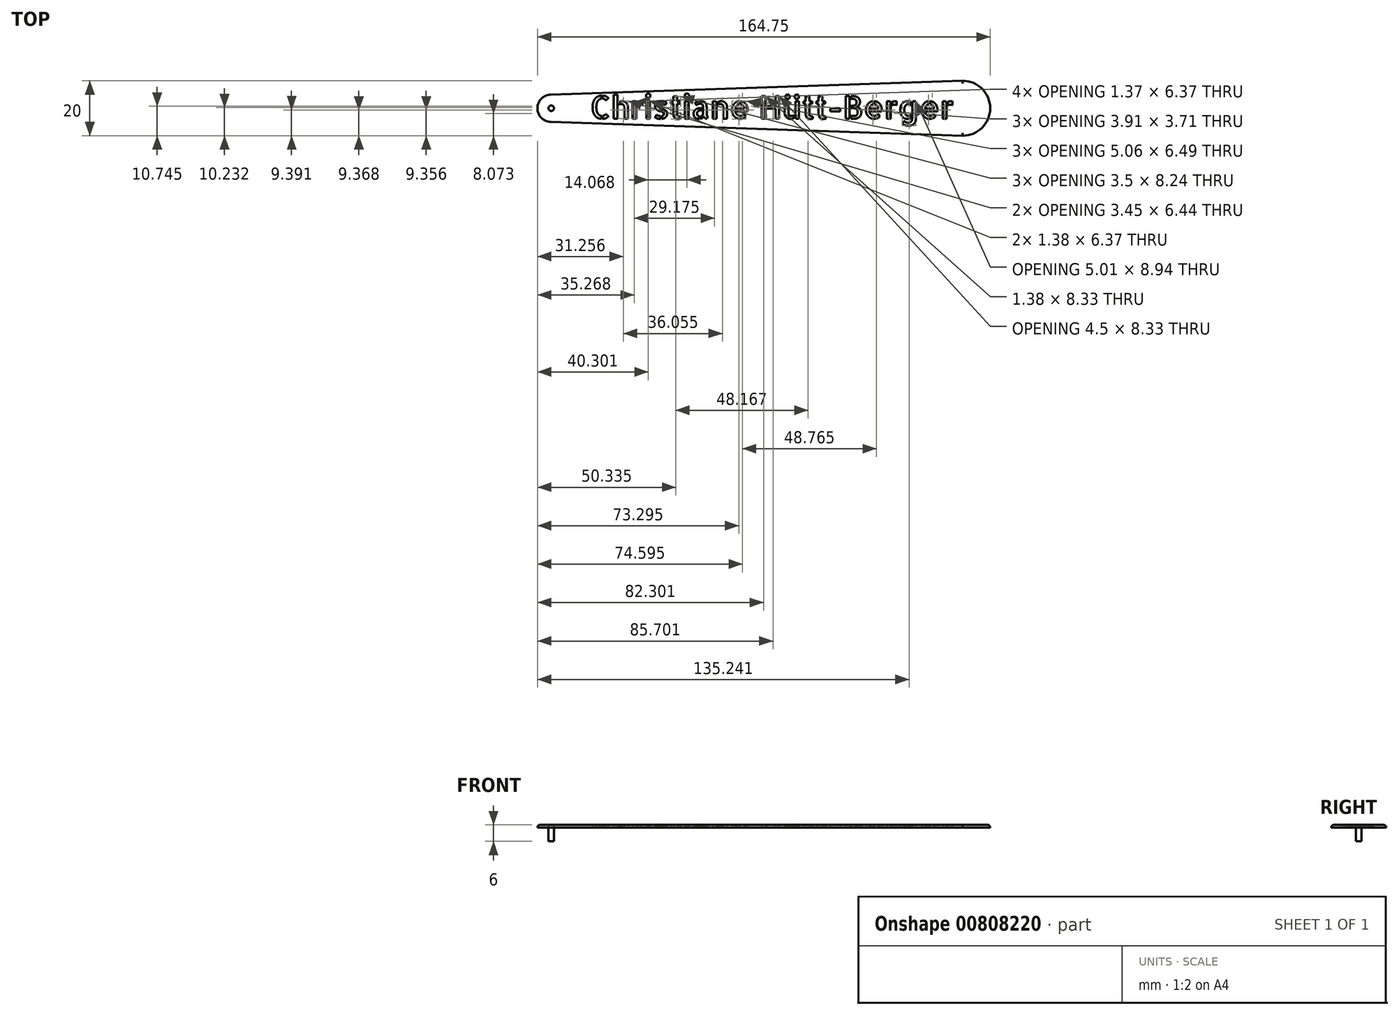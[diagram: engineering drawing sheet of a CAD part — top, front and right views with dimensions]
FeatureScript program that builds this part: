
annotation { "Feature Type Name" : "Feature", "Feature Type Description" : "" }
export const myFeature = defineFeature(function(context is Context, id is Id, definition is map)
    precondition{}
    {
        {
            var Q0;
            Q0=qCreatedBy(makeId("Top.planeOp"),FACE);
            var sketch = newSketch(context, id + "F0", { "sketchPlane" : qUnion([Q0])});
            skCircle(sketch, "E0", {"center": v(0, 0) * mm, "radius": 5 * mm});
            skLineSegment(sketch, "E1", {"start": v(0, 0) * mm, "end": v(149.75, 0) * mm, "construction": true});
            skLineSegment(sketch, "E2", {"start": v(-0.17, -5) * mm, "end": v(149.75, -10) * mm});
            skLineSegment(sketch, "E3", {"start": v(-0.17, 5) * mm, "end": v(149.75, 10) * mm});
            skLineSegment(sketch, "E4", {"start": v(149.75, 10) * mm, "end": v(149.75, -10) * mm, "construction": true});
            skArc(sketch, "E5", {"start": v(149.08, -9.98) * mm, "mid": v(159.75, 0) * mm, "end": v(149.08, 9.98) * mm});
            skCircle(sketch, "E6", {"center": v(0, 0) * mm, "radius": 1 * mm});
            skSolve(sketch);
        }
        {
            var Q0;
            Q0=makeQuery(id+"F0.imprint","IMPRINT",FACE,{"disambiguationData":[TD([[makeQuery(id+"F0.imprint","IMPRINT",EDGE,{"derivedFrom":sQuery(id+"F0.wireOp",EDGE,"AOrL48i1-m9wN-TTek-OaFp-i6hoLE5QwSDf")}),-1.0]])]});
            var Q1;
            {var subQ4=sQuery(id+"F0.wireOp",EDGE,"E0");var subQ8=sQuery(id+"F0.wireOp",EDGE,"E2");var subQ17=makeQuery(id+"F0.imprint","INTERSECT",VERTEX,{"derivedFrom":[subQ4,subQ8]});Q1=makeQuery(id+"F0.imprint","IMPRINT",FACE,{"disambiguationData":[TD([[makeQuery(id+"F0.imprint","IMPRINT",EDGE,{"disambiguationData":[TD([[subQ17,-1.0]])],"derivedFrom":subQ4}),-1.0]])]});}
            var Q2;
            {var subQ1=sQuery(id+"F0.wireOp",EDGE,"429c22a2-0887-486a-967f-2b94e1a87693");var subQ8=sQuery(id+"F0.wireOp",EDGE,"E0");var subQ9=makeQuery(id+"F0.imprint","INTERSECT",VERTEX,{"derivedFrom":[subQ8,subQ1]});Q2=makeQuery(id+"F0.imprint","IMPRINT",FACE,{"disambiguationData":[TD([[makeQuery(id+"F0.imprint","IMPRINT",EDGE,{"disambiguationData":[TD([[subQ9,-1.0]])],"derivedFrom":subQ8}),-1.0]])]});}
            var Q3;
            {var subQ0=sQuery(id+"F0.wireOp",EDGE,"9d5f52ef-638e-458b-9d80-165e25f735ae0.MirrorCS");var subQ1=sQuery(id+"F0.wireOp",EDGE,"429c22a2-0887-486a-967f-2b94e1a87693");var subQ2=makeQuery(id+"F0.imprint","INTERSECT",VERTEX,{"disambiguationData":[OD(1.0)],"derivedFrom":[subQ1,subQ0]});Q3=makeQuery(id+"F0.imprint","IMPRINT",FACE,{"disambiguationData":[TD([[makeQuery(id+"F0.imprint","IMPRINT",EDGE,{"disambiguationData":[TD([[subQ2,-1.0]])],"derivedFrom":subQ1}),-1.0]])]});}
            var Q4;
            {var subQ0=sQuery(id+"F0.wireOp",EDGE,"9d5f52ef-638e-458b-9d80-165e25f735ae0.MirrorCS");var subQ1=sQuery(id+"F0.wireOp",EDGE,"429c22a2-0887-486a-967f-2b94e1a87693");var subQ2=makeQuery(id+"F0.imprint","INTERSECT",VERTEX,{"disambiguationData":[OD(2.0)],"derivedFrom":[subQ1,subQ0]});Q4=makeQuery(id+"F0.imprint","IMPRINT",FACE,{"disambiguationData":[TD([[makeQuery(id+"F0.imprint","IMPRINT",EDGE,{"disambiguationData":[TD([[subQ2,-1.0]])],"derivedFrom":subQ1}),1.0]])]});}
            var Q5;
            {var subQ0=sQuery(id+"F0.wireOp",EDGE,"9d5f52ef-638e-458b-9d80-165e25f735ae0.MirrorCS");var subQ1=sQuery(id+"F0.wireOp",EDGE,"429c22a2-0887-486a-967f-2b94e1a87693");var subQ2=makeQuery(id+"F0.imprint","INTERSECT",VERTEX,{"disambiguationData":[OD(0.0)],"derivedFrom":[subQ1,subQ0]});Q5=makeQuery(id+"F0.imprint","IMPRINT",FACE,{"disambiguationData":[TD([[makeQuery(id+"F0.imprint","IMPRINT",EDGE,{"disambiguationData":[TD([[subQ2,1.0]])],"derivedFrom":subQ1}),-1.0]])]});}
            var Q6;
            {var subQ0=sQuery(id+"F0.wireOp",EDGE,"9f0347f5-2bf8-49b9-a686-556642ef9bf0");var subQ1=sQuery(id+"F0.wireOp",EDGE,"9d5f52ef-638e-458b-9d80-165e25f735ae0.MirrorCS");var subQ2=makeQuery(id+"F0.imprint","INTERSECT",VERTEX,{"disambiguationData":[OD(0.0)],"derivedFrom":[subQ1,subQ0]});Q6=makeQuery(id+"F0.imprint","IMPRINT",FACE,{"disambiguationData":[TD([[makeQuery(id+"F0.imprint","IMPRINT",EDGE,{"disambiguationData":[TD([[subQ2,-1.0]])],"derivedFrom":subQ1}),1.0]])]});}
            var Q7;
            {var subQ0=sQuery(id+"F0.wireOp",EDGE,"9f0347f5-2bf8-49b9-a686-556642ef9bf0");var subQ1=sQuery(id+"F0.wireOp",EDGE,"9d5f52ef-638e-458b-9d80-165e25f735ae0.MirrorCS");var subQ2=makeQuery(id+"F0.imprint","INTERSECT",VERTEX,{"disambiguationData":[OD(0.0)],"derivedFrom":[subQ1,subQ0]});Q7=makeQuery(id+"F0.imprint","IMPRINT",FACE,{"disambiguationData":[TD([[makeQuery(id+"F0.imprint","IMPRINT",EDGE,{"disambiguationData":[TD([[subQ2,-1.0]])],"derivedFrom":subQ1}),-1.0]])]});}
            var Q8;
            {var subQ0=sQuery(id+"F0.wireOp",EDGE,"981ca7ae-3106-4b93-b2f6-23ef42e42c5a");var subQ1=sQuery(id+"F0.wireOp",EDGE,"9d5f52ef-638e-458b-9d80-165e25f735ae0.MirrorCS");var subQ3=makeQuery(id+"F0.imprint","INTERSECT",VERTEX,{"derivedFrom":[subQ1,subQ0]});Q8=makeQuery(id+"F0.imprint","IMPRINT",FACE,{"disambiguationData":[TD([[makeQuery(id+"F0.imprint","IMPRINT",EDGE,{"disambiguationData":[TD([[subQ3,1.0]])],"derivedFrom":subQ1}),1.0]])]});}
            var Q9;
            {var subQ0=sQuery(id+"F0.wireOp",EDGE,"981ca7ae-3106-4b93-b2f6-23ef42e42c5a");var subQ2=sQuery(id+"F0.wireOp",EDGE,"E0");var subQ4=makeQuery(id+"F0.imprint","INTERSECT",VERTEX,{"derivedFrom":[subQ2,subQ0]});Q9=makeQuery(id+"F0.imprint","IMPRINT",FACE,{"disambiguationData":[TD([[makeQuery(id+"F0.imprint","IMPRINT",EDGE,{"disambiguationData":[TD([[subQ4,-1.0]])],"derivedFrom":subQ0}),1.0]])]});}
            var Q10;
            {var subQ0=sQuery(id+"F0.wireOp",EDGE,"981ca7ae-3106-4b93-b2f6-23ef42e42c5a");var subQ1=sQuery(id+"F0.wireOp",EDGE,"E0");var subQ3=makeQuery(id+"F0.imprint","INTERSECT",VERTEX,{"derivedFrom":[subQ1,subQ0]});Q10=makeQuery(id+"F0.imprint","IMPRINT",FACE,{"disambiguationData":[TD([[makeQuery(id+"F0.imprint","IMPRINT",EDGE,{"disambiguationData":[TD([[subQ3,-1.0]])],"derivedFrom":subQ1}),1.0]])]});}
            var Q11;
            Q11=makeQuery(id+"F0.imprint","IMPRINT",FACE,{"disambiguationData":[TD([[makeQuery(id+"F0.imprint","IMPRINT",EDGE,{"derivedFrom":sQuery(id+"F0.wireOp",EDGE,"AOrL48i1-m9wN-TTek-OaFp-i6hoLE5QwSDf")}),1.0]])]});
            extrude(context, id + "F1", {"entities" : qUnion([Q0, Q1, Q2, Q3, Q4, Q5, Q6, Q7, Q8, Q9, Q10, Q11]), "depth" : 1 * mm, "offsetDistance" : 25 * mm});
        }
        {
            var Q0;
            Q0=makeQuery(id+"F0.imprint","IMPRINT",FACE,{"disambiguationData":[TD([[makeQuery(id+"F0.imprint","IMPRINT",EDGE,{"derivedFrom":sQuery(id+"F0.wireOp",EDGE,"AOrL48i1-m9wN-TTek-OaFp-i6hoLE5QwSDf")}),1.0]])]});
            var Q1;
            Q1=makeQuery(id+"F0.imprint","IMPRINT",FACE,{"disambiguationData":[TD([[makeQuery(id+"F0.imprint","IMPRINT",EDGE,{"derivedFrom":sQuery(id+"F0.wireOp",EDGE,"AOrL48i1-m9wN-TTek-OaFp-i6hoLE5QwSDf")}),1.0]])]});
            var Q2;
            Q2=makeQuery(id+"F0.imprint","IMPRINT",FACE,{"disambiguationData":[TD([[makeQuery(id+"F0.imprint","IMPRINT",EDGE,{"derivedFrom":sQuery(id+"F0.wireOp",EDGE,"E6")}),1.0]])]});
            extrude(context, id + "F2", {"entities" : qUnion([Q0, Q1, Q2]), "operationType" : NewBodyOperationType.ADD, "oppositeDirection" : true, "depth" : 5 * mm, "offsetDistance" : 25 * mm});
        }
        {
            var Q0;
            Q0=qCreatedBy(makeId("Top.planeOp"),FACE);
            var sketch = newSketch(context, id + "F3", { "sketchPlane" : qUnion([Q0])});
            skText(sketch, "E7", { "text": "Christiane Hütt-Berger", "fontName": "AllertaStencil-Regular.ttf"});
            const initialGuessF3  = {"E7": [0.01415, -0.00383, 1, 0, 0.00833]};
            skSetInitialGuess(sketch, initialGuessF3);
            skSolve(sketch);
        }
        {
            var Q0;
            Q0=qSketchRegion(id+"F3",true);
            extrude(context, id + "F4", {"entities" : qUnion([Q0]), "operationType" : NewBodyOperationType.REMOVE, "depth" : 25 * mm, "offsetDistance" : 25 * mm});
        }
        {
            var Q0;
            Q0=makeQuery(id+"F1.opExtrude","CAP_EDGE",EDGE,{"disambiguationData":[OSD([sQuery(id+"F0.wireOp",EDGE,"E0")])],"isStart":false});
            var Q1;
            Q1=makeQuery(id+"F1.opExtrude","CAP_EDGE",EDGE,{"disambiguationData":[OSD([sQuery(id+"F0.wireOp",EDGE,"E3")])],"isStart":false});
            var Q2;
            Q2=makeQuery(id+"F1.opExtrude","CAP_EDGE",EDGE,{"disambiguationData":[OSD([sQuery(id+"F0.wireOp",EDGE,"E2")])],"isStart":false});
            var Q3;
            Q3=makeQuery(id+"F1.opExtrude","CAP_EDGE",EDGE,{"disambiguationData":[OSD([sQuery(id+"F0.wireOp",EDGE,"E5")])],"isStart":false});
            fillet(context, id + "F5", {"entities" : qUnion([Q0, Q1, Q2, Q3]), "radius" : 1 * mm, "tangentPropagation" : true, "allowEdgeOverflow" : false});
        }
    });
